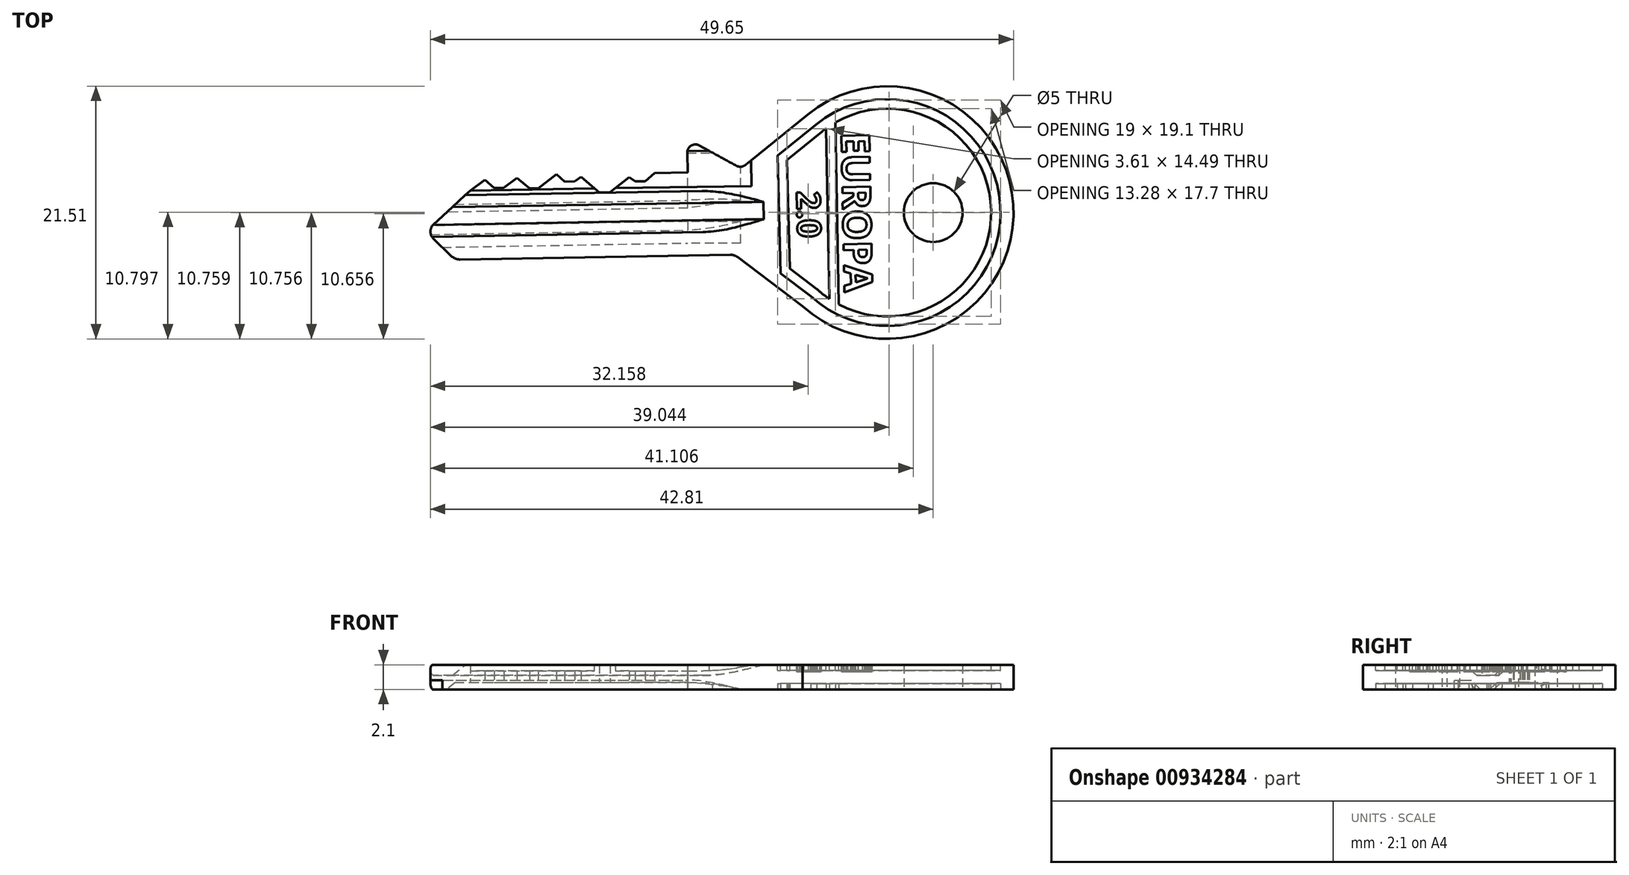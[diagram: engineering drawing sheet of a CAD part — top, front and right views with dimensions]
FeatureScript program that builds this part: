
annotation { "Feature Type Name" : "Feature", "Feature Type Description" : "" }
export const myFeature = defineFeature(function(context is Context, id is Id, definition is map)
    precondition{}
    {
        {
            var Q0;
            Q0=qCreatedBy(makeId("Top.planeOp"),FACE);
            var sketch = newSketch(context, id + "F0", { "sketchPlane" : qUnion([Q0])});
            skLineSegment(sketch, "E0", {"start": v(8, -3.49) * mm, "end": v(-15.02, -3.89) * mm});
            skLineSegment(sketch, "E1", {"start": v(-17.3, -2.08) * mm, "end": v(-15.74, -3.6) * mm});
            skPoint(sketch, "E2.visualSharp", {"position": v(-15.44, -3.9) * mm});
            skArc(sketch, "E2.filletArc", {"start": v(-15.74, -3.6) * mm, "mid": v(-15.41, -3.82) * mm, "end": v(-15.02, -3.89) * mm});
            skLineSegment(sketch, "E3", {"start": v(-14.14, 1.98) * mm, "end": v(-17.28, -0.92) * mm});
            skPoint(sketch, "E4.visualSharp", {"position": v(-17.9, -1.5) * mm});
            skArc(sketch, "E4.filletArc", {"start": v(-17.28, -0.92) * mm, "mid": v(-17.53, -1.5) * mm, "end": v(-17.3, -2.08) * mm});
            skLineSegment(sketch, "E5", {"start": v(-3.58, 2.18) * mm, "end": v(-14.14, 1.98) * mm});
            skLineSegment(sketch, "E6", {"start": v(1.54, 3.48) * mm, "end": v(4.36, 3.53) * mm});
            skLineSegment(sketch, "E7", {"start": v(4.36, 3.53) * mm, "end": v(4.33, 5.2) * mm});
            skLineSegment(sketch, "E8", {"start": v(8.52, 4.1) * mm, "end": v(5.37, 5.82) * mm});
            skPoint(sketch, "E9.visualSharp", {"position": v(4.3, 6.4) * mm});
            skArc(sketch, "E9.filletArc", {"start": v(5.37, 5.82) * mm, "mid": v(4.67, 5.8) * mm, "end": v(4.33, 5.2) * mm});
            skLineSegment(sketch, "E10", {"start": v(14.6, 8.46) * mm, "end": v(9.3, 4.16) * mm});
            skPoint(sketch, "E11.visualSharp", {"position": v(8.93, 3.87) * mm});
            skArc(sketch, "E11.filletArc", {"start": v(8.52, 4.1) * mm, "mid": v(8.92, 4.01) * mm, "end": v(9.3, 4.16) * mm});
            skLineSegment(sketch, "E12", {"start": v(15.16, -8.62) * mm, "end": v(8.63, -3.7) * mm});
            skPoint(sketch, "E13.visualSharp", {"position": v(8.35, -3.48) * mm});
            skArc(sketch, "E13.filletArc", {"start": v(8.63, -3.7) * mm, "mid": v(8.33, -3.54) * mm, "end": v(8, -3.49) * mm});
            skLineSegment(sketch, "E14", {"start": v(-0.61, 3.12) * mm, "end": v(-0.1, 2.75) * mm});
            skLineSegment(sketch, "E15", {"start": v(-0.1, 2.75) * mm, "end": v(0.75, 2.77) * mm});
            skLineSegment(sketch, "E16", {"start": v(0.75, 2.77) * mm, "end": v(1.54, 3.48) * mm});
            skLineSegment(sketch, "E17", {"start": v(-0.61, 3.12) * mm, "end": v(-2.21, 1.84) * mm});
            skLineSegment(sketch, "E18", {"start": v(-2.21, 1.84) * mm, "end": v(-3.15, 1.82) * mm});
            skLineSegment(sketch, "E19", {"start": v(-3.15, 1.82) * mm, "end": v(-4.72, 3.14) * mm});
            skLineSegment(sketch, "E20", {"start": v(-4.72, 3.14) * mm, "end": v(-5.24, 2.76) * mm});
            skLineSegment(sketch, "E21", {"start": v(-5.24, 2.76) * mm, "end": v(-6.1, 2.74) * mm});
            skLineSegment(sketch, "E22", {"start": v(-6.1, 2.74) * mm, "end": v(-6.8, 3.38) * mm});
            skLineSegment(sketch, "E23", {"start": v(-6.8, 3.38) * mm, "end": v(-8.35, 2.17) * mm});
            skLineSegment(sketch, "E24", {"start": v(-8.35, 2.17) * mm, "end": v(-9.1, 2.16) * mm});
            skLineSegment(sketch, "E25", {"start": v(-9.1, 2.16) * mm, "end": v(-10.17, 3.05) * mm});
            skLineSegment(sketch, "E26", {"start": v(-10.17, 3.05) * mm, "end": v(-11.26, 2.22) * mm});
            skLineSegment(sketch, "E27", {"start": v(-11.26, 2.22) * mm, "end": v(-12.1, 2.2) * mm});
            skLineSegment(sketch, "E28", {"start": v(-12.1, 2.2) * mm, "end": v(-12.9, 2.9) * mm});
            skLineSegment(sketch, "E29", {"start": v(-12.9, 2.9) * mm, "end": v(-14.14, 1.98) * mm});
            skArc(sketch, "E30", {"start": v(14.6, 8.46) * mm, "mid": v(32.11, -0.2) * mm, "end": v(14.15, -7.86) * mm});
            skCircle(sketch, "E31", {"center": v(25.28, 0.1) * mm, "radius": 2.5 * mm});
            skArc(sketch, "E32.0", {"start": v(15.3, 7.6) * mm, "mid": v(31.01, -0.18) * mm, "end": v(14.85, -7.01) * mm});
            skLineSegment(sketch, "E32.1", {"start": v(15.3, 7.6) * mm, "end": v(12.01, 4.95) * mm});
            skLineSegment(sketch, "E33.0", {"start": v(14.85, -7.01) * mm, "end": v(12.3, -5.08) * mm});
            skLineSegment(sketch, "E34", {"start": v(12.01, 4.95) * mm, "end": v(12.3, -5.08) * mm});
            skLineSegment(sketch, "E35", {"start": v(16.13, 8.21) * mm, "end": v(16.45, -8.2) * mm});
            skSolve(sketch);
        }
        {
            var Q0;
            Q0 = qSketchRegion(id + "F0", true);
            var Q1;
            Q1=makeQuery(id+"F0.imprint","IMPRINT",FACE,{"disambiguationData":[TD([[makeQuery(id+"F0.imprint","IMPRINT",EDGE,{"derivedFrom":sQuery(id+"F0.wireOp",EDGE,"E31")}),-1.0]])]});
            var Q2;
            {var subQ1=sQuery(id+"F0.wireOp",EDGE,"E32.1");Q2=makeQuery(id+"F0.imprint","IMPRINT",FACE,{"disambiguationData":[TD([[makeQuery(id+"F0.imprint","IMPRINT",EDGE,{"derivedFrom":subQ1}),1.0]])]});}
            extrude(context, id + "F1", {"entities" : qUnion([Q0, Q1, Q2]), "depth" : 2.1 * mm, "offsetDistance" : 25 * mm});
        }
        {
            var Q0;
            Q0=qCreatedBy(makeId("Top.planeOp"),FACE);
            var sketch = newSketch(context, id + "F2", { "sketchPlane" : qUnion([Q0])});
            skPoint(sketch, "E36.0", {"position": v(16.29, 0) * mm});
            skLineSegment(sketch, "E37.0", {"start": v(12.01, 4.95) * mm, "end": v(12.3, -5.08) * mm});
            skLineSegment(sketch, "E38.0", {"start": v(16.15, 7.25) * mm, "end": v(16.43, -7.24) * mm});
            skLineSegment(sketch, "E39.0", {"start": v(15.3, 7.6) * mm, "end": v(12.01, 4.95) * mm});
            skArc(sketch, "E40.0", {"start": v(15.3, 7.6) * mm, "mid": v(31.01, -0.18) * mm, "end": v(14.85, -7.01) * mm});
            skLineSegment(sketch, "E41.0", {"start": v(14.85, -7.01) * mm, "end": v(12.3, -5.08) * mm});
            skArc(sketch, "E42.0", {"start": v(15.8, 6.98) * mm, "mid": v(15.97, 7.12) * mm, "end": v(16.15, 7.25) * mm});
            skLineSegment(sketch, "E42.1", {"start": v(15.8, 6.98) * mm, "end": v(12.82, 4.58) * mm});
            skLineSegment(sketch, "E42.2", {"start": v(12.82, 4.58) * mm, "end": v(13.08, -4.67) * mm});
            skLineSegment(sketch, "E42.3", {"start": v(15.36, -6.4) * mm, "end": v(13.08, -4.67) * mm});
            skLineSegment(sketch, "E43.0", {"start": v(16.94, 7.77) * mm, "end": v(17.24, -7.72) * mm});
            skPoint(sketch, "E44.orphan", {"position": v(16.13, 8.21) * mm});
            skArc(sketch, "E45.trimOffspring", {"start": v(16.94, 7.77) * mm, "mid": v(30.22, 0.28) * mm, "end": v(17.24, -7.72) * mm});
            skPoint(sketch, "E46.orphan", {"position": v(16.45, -8.2) * mm});
            skArc(sketch, "E47.trimOffspring", {"start": v(16.43, -7.24) * mm, "mid": v(15.88, -6.84) * mm, "end": v(15.36, -6.4) * mm});
            skText(sketch, "E48", { "text": "EUROPA", "fontName": "OpenSans-Bold.ttf"});
            skLineSegment(sketch, "E49", {"start": v(17.35, 11.93) * mm, "end": v(17.85, -13.3) * mm, "construction": true});
            skPoint(sketch, "E50", {"position": v(17.45, 6.98) * mm});
            skText(sketch, "E51", { "text": "2.0", "fontName": "OpenSans-Bold.ttf"});
            skPoint(sketch, "E52", {"position": v(12.88, 2.46) * mm});
            const initialGuessF2  = {"E48": [0.01745, 0.00698, 0.01969, -0.9998, 0.0024], "E51": [0.01288, 0.00246, 0.0276, -0.99962, 0.0024]};
            skSetInitialGuess(sketch, initialGuessF2);
            skSolve(sketch);
        }
        {
            var Q0;
            Q0 = qSketchRegion(id + "F2", true);
            extrude(context, id + "F3", {"entities" : qUnion([Q0]), "operationType" : NewBodyOperationType.REMOVE, "depth" : 0.5 * mm, "offsetDistance" : 25 * mm});
        }
        {
            var Q0;
            Q0=makeQuery(id+"F1.opExtrude","CAP_FACE",FACE,{"disambiguationData":[OSD([sQuery(id+"F0.wireOp",EDGE,"E0"),sQuery(id+"F0.wireOp",EDGE,"E1"),sQuery(id+"F0.wireOp",EDGE,"E2.filletArc"),sQuery(id+"F0.wireOp",EDGE,"E3"),sQuery(id+"F0.wireOp",EDGE,"E4.filletArc"),sQuery(id+"F0.wireOp",EDGE,"E6"),sQuery(id+"F0.wireOp",EDGE,"E7"),sQuery(id+"F0.wireOp",EDGE,"E8"),sQuery(id+"F0.wireOp",EDGE,"E9.filletArc"),sQuery(id+"F0.wireOp",EDGE,"E10"),sQuery(id+"F0.wireOp",EDGE,"E11.filletArc"),sQuery(id+"F0.wireOp",EDGE,"E12"),sQuery(id+"F0.wireOp",EDGE,"E13.filletArc"),sQuery(id+"F0.wireOp",EDGE,"E14"),sQuery(id+"F0.wireOp",EDGE,"E15"),sQuery(id+"F0.wireOp",EDGE,"E16"),sQuery(id+"F0.wireOp",EDGE,"E17"),sQuery(id+"F0.wireOp",EDGE,"E18"),sQuery(id+"F0.wireOp",EDGE,"E19"),sQuery(id+"F0.wireOp",EDGE,"E20"),sQuery(id+"F0.wireOp",EDGE,"E21"),sQuery(id+"F0.wireOp",EDGE,"E22"),sQuery(id+"F0.wireOp",EDGE,"E23"),sQuery(id+"F0.wireOp",EDGE,"E24"),sQuery(id+"F0.wireOp",EDGE,"E25"),sQuery(id+"F0.wireOp",EDGE,"E26"),sQuery(id+"F0.wireOp",EDGE,"E27"),sQuery(id+"F0.wireOp",EDGE,"E28"),sQuery(id+"F0.wireOp",EDGE,"E29"),sQuery(id+"F0.wireOp",EDGE,"E30"),sQuery(id+"F0.wireOp",EDGE,"E31")])],"isStart":false});
            var sketch = newSketch(context, id + "F4", { "sketchPlane" : qUnion([Q0])});
            skArc(sketch, "E53.0", {"start": v(15.3, 7.6) * mm, "mid": v(31.01, -0.18) * mm, "end": v(14.85, -7.01) * mm});
            skArc(sketch, "E54.0", {"start": v(16.94, 7.77) * mm, "mid": v(30.22, 0.28) * mm, "end": v(17.24, -7.72) * mm});
            skLineSegment(sketch, "E55.0", {"start": v(15.3, 7.6) * mm, "end": v(12.01, 4.95) * mm});
            skLineSegment(sketch, "E56.0", {"start": v(12.01, 4.95) * mm, "end": v(12.3, -5.08) * mm});
            skLineSegment(sketch, "E57.0", {"start": v(14.85, -7.01) * mm, "end": v(12.3, -5.08) * mm});
            skLineSegment(sketch, "E58.0", {"start": v(12.82, 4.58) * mm, "end": v(13.08, -4.67) * mm});
            skLineSegment(sketch, "E59.0", {"start": v(15.36, -6.4) * mm, "end": v(13.08, -4.67) * mm});
            skLineSegment(sketch, "E60.0", {"start": v(15.8, 6.98) * mm, "end": v(12.82, 4.58) * mm});
            skLineSegment(sketch, "E61.0", {"start": v(16.15, 7.25) * mm, "end": v(16.43, -7.24) * mm});
            skArc(sketch, "E62.0", {"start": v(16.43, -7.24) * mm, "mid": v(15.88, -6.84) * mm, "end": v(15.36, -6.4) * mm});
            skArc(sketch, "E63.0", {"start": v(15.8, 6.98) * mm, "mid": v(15.97, 7.12) * mm, "end": v(16.15, 7.25) * mm});
            skLineSegment(sketch, "E64.0", {"start": v(16.94, 7.77) * mm, "end": v(17.24, -7.72) * mm});
            skSolve(sketch);
        }
        {
            var Q0;
            Q0 = qSketchRegion(id + "F4", true);
            extrude(context, id + "F5", {"entities" : qUnion([Q0]), "operationType" : NewBodyOperationType.REMOVE, "oppositeDirection" : true, "depth" : 0.5 * mm, "offsetDistance" : 25 * mm});
        }
        {
            var Q0;
            {var subQ0=sQuery(id+"F0.wireOp",EDGE,"E21");var subQ1=sQuery(id+"F0.wireOp",EDGE,"E20");var subQ2=sQuery(id+"F0.wireOp",EDGE,"E19");var subQ3=sQuery(id+"F0.wireOp",EDGE,"E18");var subQ4=sQuery(id+"F0.wireOp",EDGE,"E17");var subQ5=sQuery(id+"F0.wireOp",EDGE,"E16");var subQ6=sQuery(id+"F0.wireOp",EDGE,"E15");var subQ7=sQuery(id+"F0.wireOp",EDGE,"E14");var subQ8=sQuery(id+"F0.wireOp",EDGE,"E13.filletArc");var subQ9=sQuery(id+"F0.wireOp",EDGE,"E12");var subQ10=sQuery(id+"F0.wireOp",EDGE,"E11.filletArc");var subQ11=sQuery(id+"F0.wireOp",EDGE,"E2.filletArc");var subQ12=sQuery(id+"F0.wireOp",EDGE,"E1");var subQ13=sQuery(id+"F0.wireOp",EDGE,"E3");var subQ14=sQuery(id+"F0.wireOp",EDGE,"E22");var subQ15=sQuery(id+"F0.wireOp",EDGE,"E0");var subQ16=sQuery(id+"F0.wireOp",EDGE,"E10");var subQ17=sQuery(id+"F0.wireOp",EDGE,"E4.filletArc");var subQ18=sQuery(id+"F0.wireOp",EDGE,"E6");var subQ19=sQuery(id+"F0.wireOp",EDGE,"E7");var subQ20=sQuery(id+"F0.wireOp",EDGE,"E8");var subQ21=sQuery(id+"F0.wireOp",EDGE,"E9.filletArc");var subQ22=sQuery(id+"F0.wireOp",EDGE,"E23");var subQ23=sQuery(id+"F0.wireOp",EDGE,"E24");var subQ24=sQuery(id+"F0.wireOp",EDGE,"E25");var subQ25=sQuery(id+"F0.wireOp",EDGE,"E26");var subQ26=sQuery(id+"F0.wireOp",EDGE,"E27");var subQ27=sQuery(id+"F0.wireOp",EDGE,"E28");var subQ28=sQuery(id+"F0.wireOp",EDGE,"E29");var subQ29=sQuery(id+"F0.wireOp",EDGE,"E30");Q0=makeQuery(id+"F5.boolean.opBoolean","SPLIT",FACE,{"disambiguationData":[TD([makeQuery(id+"F1.opExtrude","SWEPT_FACE",FACE,{"disambiguationData":[OSD([subQ15])]})])],"derivedFrom":makeQuery(id+"F1.opExtrude","CAP_FACE",FACE,{"disambiguationData":[OSD([subQ15,subQ12,subQ11,subQ13,subQ17,subQ18,subQ19,subQ20,subQ21,subQ16,subQ10,subQ9,subQ8,subQ7,subQ6,subQ5,subQ4,subQ3,subQ2,subQ1,subQ0,subQ14,subQ22,subQ23,subQ24,subQ25,subQ26,subQ27,subQ28,subQ29,sQuery(id+"F0.wireOp",EDGE,"E31")])],"isStart":false})});}
            var sketch = newSketch(context, id + "F6", { "sketchPlane" : qUnion([Q0])});
            skLineSegment(sketch, "E65", {"start": v(-22.93, -1.04) * mm, "end": v(5.65, -0.55) * mm});
            skLineSegment(sketch, "E66", {"start": v(5.65, -0.55) * mm, "end": v(5.63, 0.93) * mm});
            skLineSegment(sketch, "E67", {"start": v(5.63, 0.93) * mm, "end": v(-22.93, 0.44) * mm});
            skLineSegment(sketch, "E68", {"start": v(-22.93, 0.44) * mm, "end": v(-22.93, -1.04) * mm});
            skSolve(sketch);
        }
        {
            var Q0;
            {var subQ0=sQuery(id+"F0.wireOp",EDGE,"E21");var subQ1=sQuery(id+"F0.wireOp",EDGE,"E20");var subQ2=sQuery(id+"F0.wireOp",EDGE,"E19");var subQ3=sQuery(id+"F0.wireOp",EDGE,"E18");var subQ4=sQuery(id+"F0.wireOp",EDGE,"E17");var subQ5=sQuery(id+"F0.wireOp",EDGE,"E16");var subQ6=sQuery(id+"F0.wireOp",EDGE,"E15");var subQ7=sQuery(id+"F0.wireOp",EDGE,"E14");var subQ8=sQuery(id+"F0.wireOp",EDGE,"E13.filletArc");var subQ9=sQuery(id+"F0.wireOp",EDGE,"E12");var subQ10=sQuery(id+"F0.wireOp",EDGE,"E11.filletArc");var subQ11=sQuery(id+"F0.wireOp",EDGE,"E2.filletArc");var subQ12=sQuery(id+"F0.wireOp",EDGE,"E1");var subQ13=sQuery(id+"F0.wireOp",EDGE,"E3");var subQ14=sQuery(id+"F0.wireOp",EDGE,"E22");var subQ15=sQuery(id+"F0.wireOp",EDGE,"E0");var subQ16=sQuery(id+"F0.wireOp",EDGE,"E10");var subQ17=sQuery(id+"F0.wireOp",EDGE,"E4.filletArc");var subQ18=sQuery(id+"F0.wireOp",EDGE,"E6");var subQ19=sQuery(id+"F0.wireOp",EDGE,"E7");var subQ20=sQuery(id+"F0.wireOp",EDGE,"E8");var subQ21=sQuery(id+"F0.wireOp",EDGE,"E9.filletArc");var subQ22=sQuery(id+"F0.wireOp",EDGE,"E23");var subQ23=sQuery(id+"F0.wireOp",EDGE,"E24");var subQ24=sQuery(id+"F0.wireOp",EDGE,"E25");var subQ25=sQuery(id+"F0.wireOp",EDGE,"E26");var subQ26=sQuery(id+"F0.wireOp",EDGE,"E27");var subQ27=sQuery(id+"F0.wireOp",EDGE,"E28");var subQ28=sQuery(id+"F0.wireOp",EDGE,"E29");var subQ29=sQuery(id+"F0.wireOp",EDGE,"E30");Q0=makeQuery(id+"F5.boolean.opBoolean","SPLIT",FACE,{"disambiguationData":[TD([makeQuery(id+"F1.opExtrude","SWEPT_FACE",FACE,{"disambiguationData":[OSD([subQ15])]})])],"derivedFrom":makeQuery(id+"F1.opExtrude","CAP_FACE",FACE,{"disambiguationData":[OSD([subQ15,subQ12,subQ11,subQ13,subQ17,subQ18,subQ19,subQ20,subQ21,subQ16,subQ10,subQ9,subQ8,subQ7,subQ6,subQ5,subQ4,subQ3,subQ2,subQ1,subQ0,subQ14,subQ22,subQ23,subQ24,subQ25,subQ26,subQ27,subQ28,subQ29,sQuery(id+"F0.wireOp",EDGE,"E31")])],"isStart":false})});}
            var sketch = newSketch(context, id + "F7", { "sketchPlane" : qUnion([Q0])});
            skLineSegment(sketch, "E69", {"start": v(-14.65, 1.98) * mm, "end": v(4.42, 2.28) * mm});
            skLineSegment(sketch, "E70", {"start": v(4.42, 2.28) * mm, "end": v(4.35, 6.53) * mm});
            skLineSegment(sketch, "E71", {"start": v(4.35, 6.53) * mm, "end": v(-14.58, 4.95) * mm});
            skLineSegment(sketch, "E72", {"start": v(-14.58, 4.95) * mm, "end": v(-14.65, 1.98) * mm});
            skSolve(sketch);
        }
        {
            var Q0;
            Q0 = qSketchRegion(id + "F7", true);
            extrude(context, id + "F8", {"entities" : qUnion([Q0]), "operationType" : NewBodyOperationType.REMOVE, "oppositeDirection" : true, "depth" : 0.52 * mm, "offsetDistance" : 25 * mm});
        }
        {
            var Q0;
            {var subQ0=sQuery(id+"F0.wireOp",EDGE,"E17");var subQ2=sQuery(id+"F7.wireOp",EDGE,"E69");Q0=makeQuery(id+"F8.boolean.opBoolean","COPY",FACE,{"disambiguationData":[TD([makeQuery(id+"F1.opExtrude","SWEPT_FACE",FACE,{"disambiguationData":[OSD([subQ0])]})])],"derivedFrom":makeQuery(id+"F8.opExtrude","SWEPT_FACE",FACE,{"disambiguationData":[OSD([subQ2])]})});}
            var sketch = newSketch(context, id + "F9", { "sketchPlane" : qUnion([Q0])});
            skLineSegment(sketch, "E73.0", {"start": v(-4.45, 1.58) * mm, "end": v(-4.45, 2.1) * mm});
            skLineSegment(sketch, "E74", {"start": v(-4.45, 1.58) * mm, "end": v(-9.85, 1.58) * mm});
            skLineSegment(sketch, "E75", {"start": v(-4.45, 2.1) * mm, "end": v(-4.45, 2.45) * mm});
            skLineSegment(sketch, "E76", {"start": v(-4.45, 2.45) * mm, "end": v(-9.85, 2.62) * mm});
            skLineSegment(sketch, "E77", {"start": v(-9.85, 2.62) * mm, "end": v(-9.85, 1.58) * mm});
            skPoint(sketch, "E78", {"position": v(-9.85, 2.1) * mm});
            skFitSpline(sketch, "E79", {"points": [v(-4.45, 1.58) * mm, v(-9.85, 2.1) * mm], "startDerivative": vector(-6.66, 0) * mm, "endDerivative": vector(-5.03, 1.26) * mm});
            skSolve(sketch);
        }
        {
            var Q0;
            Q0=makeQuery(id+"F9.imprint","IMPRINT",FACE,{"disambiguationData":[TD([[makeQuery(id+"F9.imprint","IMPRINT",EDGE,{"derivedFrom":sQuery(id+"F9.wireOp",EDGE,"E73.0")}),1.0]])]});
            extrude(context, id + "F10", {"entities" : qUnion([Q0]), "operationType" : NewBodyOperationType.REMOVE, "depth" : 3.06 * mm, "offsetDistance" : 25 * mm});
        }
        {
            var Q0;
            {var subQ0=sQuery(id+"F0.wireOp",EDGE,"E21");var subQ1=sQuery(id+"F0.wireOp",EDGE,"E20");var subQ2=sQuery(id+"F0.wireOp",EDGE,"E19");var subQ3=sQuery(id+"F0.wireOp",EDGE,"E18");var subQ4=sQuery(id+"F0.wireOp",EDGE,"E17");var subQ5=sQuery(id+"F0.wireOp",EDGE,"E16");var subQ6=sQuery(id+"F0.wireOp",EDGE,"E15");var subQ7=sQuery(id+"F0.wireOp",EDGE,"E14");var subQ8=sQuery(id+"F0.wireOp",EDGE,"E13.filletArc");var subQ9=sQuery(id+"F0.wireOp",EDGE,"E12");var subQ10=sQuery(id+"F0.wireOp",EDGE,"E11.filletArc");var subQ11=sQuery(id+"F0.wireOp",EDGE,"E2.filletArc");var subQ12=sQuery(id+"F0.wireOp",EDGE,"E1");var subQ13=sQuery(id+"F0.wireOp",EDGE,"E3");var subQ14=sQuery(id+"F0.wireOp",EDGE,"E22");var subQ15=sQuery(id+"F0.wireOp",EDGE,"E0");var subQ16=sQuery(id+"F0.wireOp",EDGE,"E10");var subQ17=sQuery(id+"F0.wireOp",EDGE,"E4.filletArc");var subQ18=sQuery(id+"F0.wireOp",EDGE,"E6");var subQ19=sQuery(id+"F0.wireOp",EDGE,"E7");var subQ20=sQuery(id+"F0.wireOp",EDGE,"E8");var subQ21=sQuery(id+"F0.wireOp",EDGE,"E9.filletArc");var subQ22=sQuery(id+"F0.wireOp",EDGE,"E23");var subQ23=sQuery(id+"F0.wireOp",EDGE,"E24");var subQ24=sQuery(id+"F0.wireOp",EDGE,"E25");var subQ25=sQuery(id+"F0.wireOp",EDGE,"E26");var subQ26=sQuery(id+"F0.wireOp",EDGE,"E27");var subQ27=sQuery(id+"F0.wireOp",EDGE,"E28");var subQ28=sQuery(id+"F0.wireOp",EDGE,"E29");var subQ29=sQuery(id+"F0.wireOp",EDGE,"E30");Q0=makeQuery(id+"F3.boolean.opBoolean","SPLIT",FACE,{"disambiguationData":[TD([makeQuery(id+"F1.opExtrude","SWEPT_FACE",FACE,{"disambiguationData":[OSD([subQ15])]})])],"derivedFrom":makeQuery(id+"F1.opExtrude","CAP_FACE",FACE,{"disambiguationData":[OSD([subQ15,subQ12,subQ11,subQ13,subQ17,subQ18,subQ19,subQ20,subQ21,subQ16,subQ10,subQ9,subQ8,subQ7,subQ6,subQ5,subQ4,subQ3,subQ2,subQ1,subQ0,subQ14,subQ22,subQ23,subQ24,subQ25,subQ26,subQ27,subQ28,subQ29,sQuery(id+"F0.wireOp",EDGE,"E31")])],"isStart":true})});}
            var sketch = newSketch(context, id + "F11", { "sketchPlane" : qUnion([Q0])});
            skArc(sketch, "E80.0", {"start": v(5.37, -5.82) * mm, "mid": v(4.67, -5.8) * mm, "end": v(4.33, -5.2) * mm});
            skLineSegment(sketch, "E81", {"start": v(1.71, -5.85) * mm, "end": v(7.72, -5.95) * mm, "construction": true});
            skLineSegment(sketch, "E82", {"start": v(1.2, -4.59) * mm, "end": v(8.54, -4.72) * mm, "construction": true});
            skLineSegment(sketch, "E83.0", {"start": v(4.36, -3.53) * mm, "end": v(4.33, -5.2) * mm});
            skLineSegment(sketch, "E84", {"start": v(4.35, -4.36) * mm, "end": v(-15.49, -4.02) * mm});
            skLineSegment(sketch, "E85", {"start": v(-15.49, -4.02) * mm, "end": v(-15.42, -0.8) * mm});
            skLineSegment(sketch, "E86", {"start": v(-15.42, -0.8) * mm, "end": v(4.36, -1.14) * mm});
            skLineSegment(sketch, "E87", {"start": v(4.36, -1.14) * mm, "end": v(4.36, -3.53) * mm});
            skLineSegment(sketch, "E88", {"start": v(4.36, -1.14) * mm, "end": v(7, -2.33) * mm});
            skLineSegment(sketch, "E89", {"start": v(7, -2.33) * mm, "end": v(7, -4.93) * mm});
            skLineSegment(sketch, "E90.0", {"start": v(8.52, -4.1) * mm, "end": v(5.37, -5.82) * mm});
            skLineSegment(sketch, "E91", {"start": v(7, -4.93) * mm, "end": v(4.34, -4.88) * mm});
            skSolve(sketch);
        }
        {
            var Q0;
            {var subQ2=sQuery(id+"F11.wireOp",EDGE,"E84");Q0=makeQuery(id+"F11.imprint","IMPRINT",FACE,{"disambiguationData":[TD([[makeQuery(id+"F11.imprint","IMPRINT",EDGE,{"derivedFrom":subQ2}),-1.0]])]});}
            var Q1;
            {var subQ0=sQuery(id+"F11.wireOp",EDGE,"E87");Q1=makeQuery(id+"F11.imprint","IMPRINT",FACE,{"disambiguationData":[TD([[makeQuery(id+"F11.imprint","IMPRINT",EDGE,{"derivedFrom":subQ0}),-1.0]])]});}
            extrude(context, id + "F12", {"entities" : qUnion([Q0, Q1]), "operationType" : NewBodyOperationType.REMOVE, "oppositeDirection" : true, "depth" : 0.59 * mm, "offsetDistance" : 25 * mm});
        }
        {
            var Q0;
            Q0 = qSketchRegion(id + "F6", true);
            extrude(context, id + "F13", {"entities" : qUnion([Q0]), "operationType" : NewBodyOperationType.REMOVE, "oppositeDirection" : true, "depth" : 0.91 * mm, "offsetDistance" : 25 * mm});
        }
        {
            var Q0;
            Q0=makeQuery(id+"F13.boolean.opBoolean","COPY",FACE,{"derivedFrom":makeQuery(id+"F13.opExtrude","SWEPT_FACE",FACE,{"disambiguationData":[OSD([sQuery(id+"F6.wireOp",EDGE,"E66")])]})});
            var sketch = newSketch(context, id + "F14", { "sketchPlane" : qUnion([Q0])});
            skLineSegment(sketch, "E92.0", {"start": v(-0.83, 1.2) * mm, "end": v(-0.83, 2.1) * mm});
            skLineSegment(sketch, "E93.0", {"start": v(0.65, 1.2) * mm, "end": v(0.65, 2.1) * mm});
            skLineSegment(sketch, "E94", {"start": v(-0.83, 2.1) * mm, "end": v(-1.83, 2.1) * mm});
            skLineSegment(sketch, "E95", {"start": v(0.65, 2.1) * mm, "end": v(1.65, 2.1) * mm});
            skLineSegment(sketch, "E96", {"start": v(-0.83, 1.2) * mm, "end": v(-1.83, 2.1) * mm});
            skLineSegment(sketch, "E97", {"start": v(0.65, 1.2) * mm, "end": v(1.65, 2.1) * mm});
            skSolve(sketch);
        }
        {
            var Q0;
            Q0 = qSketchRegion(id + "F14", true);
            extrude(context, id + "F15", {"entities" : qUnion([Q0]), "operationType" : NewBodyOperationType.REMOVE, "depth" : 40 * mm, "offsetDistance" : 25 * mm});
        }
        {
            var Q0;
            Q0=makeQuery(id+"F15.boolean.opBoolean","MERGE",FACE,{"derivedFrom":[makeQuery(id+"F13.boolean.opBoolean","COPY",FACE,{"derivedFrom":makeQuery(id+"F13.opExtrude","SWEPT_FACE",FACE,{"disambiguationData":[OSD([sQuery(id+"F6.wireOp",EDGE,"E66")])]})})],"fromTools":[makeQuery(id+"F15.opExtrude","CAP_FACE",FACE,{"disambiguationData":[OSD([sQuery(id+"F14.wireOp",EDGE,"E92.0"),sQuery(id+"F14.wireOp",EDGE,"E94"),sQuery(id+"F14.wireOp",EDGE,"E96")])],"isStart":true}),makeQuery(id+"F15.opExtrude","CAP_FACE",FACE,{"disambiguationData":[OSD([sQuery(id+"F14.wireOp",EDGE,"E93.0"),sQuery(id+"F14.wireOp",EDGE,"E95"),sQuery(id+"F14.wireOp",EDGE,"E97")])],"isStart":true})]});
            cPlane(context, id + "F16", {"entities" : qUnion([Q0]), "cplaneType" : CPlaneType.OFFSET, "offset" : 5.2 * mm, "oppositeDirection" : true, "width" : 150 * mm, "height" : 150 * mm});
        }
        {
            var Q0;
            Q0=qCreatedBy(id+"F16.planeOp",FACE);
            var sketch = newSketch(context, id + "F17", { "sketchPlane" : qUnion([Q0])});
            skLineSegment(sketch, "E98.0", {"start": v(0.65, 2.1) * mm, "end": v(-0.83, 2.1) * mm});
            skLineSegment(sketch, "E99", {"start": v(-0.83, 2.1) * mm, "end": v(-1.83, 3.01) * mm});
            skLineSegment(sketch, "E100", {"start": v(-1.83, 3.01) * mm, "end": v(1.65, 3.01) * mm});
            skLineSegment(sketch, "E101", {"start": v(1.65, 3.01) * mm, "end": v(0.65, 2.1) * mm});
            skLineSegment(sketch, "E102.0", {"start": v(0.65, 1.2) * mm, "end": v(-0.83, 1.2) * mm});
            skLineSegment(sketch, "E103", {"start": v(-0.83, 0.8) * mm, "end": v(-0.83, 3.67) * mm, "construction": true});
            skSolve(sketch);
        }
        {
            var Q0;
            Q0=makeQuery(id+"F15.boolean.opBoolean","MERGE",FACE,{"derivedFrom":[makeQuery(id+"F13.boolean.opBoolean","COPY",FACE,{"derivedFrom":makeQuery(id+"F13.opExtrude","SWEPT_FACE",FACE,{"disambiguationData":[OSD([sQuery(id+"F6.wireOp",EDGE,"E66")])]})})],"fromTools":[makeQuery(id+"F15.opExtrude","CAP_FACE",FACE,{"disambiguationData":[OSD([sQuery(id+"F14.wireOp",EDGE,"E92.0"),sQuery(id+"F14.wireOp",EDGE,"E94"),sQuery(id+"F14.wireOp",EDGE,"E96")])],"isStart":true}),makeQuery(id+"F15.opExtrude","CAP_FACE",FACE,{"disambiguationData":[OSD([sQuery(id+"F14.wireOp",EDGE,"E93.0"),sQuery(id+"F14.wireOp",EDGE,"E95"),sQuery(id+"F14.wireOp",EDGE,"E97")])],"isStart":true})]});
            var sketch = newSketch(context, id + "F18", { "sketchPlane" : qUnion([Q0])});
            skLineSegment(sketch, "E104.0", {"start": v(-0.83, 1.2) * mm, "end": v(-1.83, 2.1) * mm});
            skLineSegment(sketch, "E105.0", {"start": v(1.65, 2.1) * mm, "end": v(-1.83, 2.1) * mm});
            skLineSegment(sketch, "E106.0", {"start": v(0.65, 1.2) * mm, "end": v(-0.83, 1.2) * mm});
            skLineSegment(sketch, "E107.0", {"start": v(0.65, 1.19) * mm, "end": v(1.65, 2.1) * mm});
            skSolve(sketch);
        }
        {
            var Q1;
            Q1 = qSketchRegion(id + "F18", true);
            var Q2;
            Q2 = qSketchRegion(id + "F17", true);
            loft(context, id + "F19", {"operationType" : NewBodyOperationType.REMOVE, "startCondition" : LoftEndDerivativeType.NORMAL_TO_PROFILE, "startMagnitude" : 1, "sheetProfilesArray" : [{ "sheetProfileEntities" : qUnion([Q1]) }, { "sheetProfileEntities" : qUnion([Q2]) }]});
        }
        {
            var Q0;
            Q0=makeQuery(id+"F12.boolean.opBoolean","COPY",FACE,{"derivedFrom":makeQuery(id+"F12.opExtrude","CAP_FACE",FACE,{"disambiguationData":[OSD([sQuery(id+"F11.wireOp",EDGE,"E83.0"),sQuery(id+"F11.wireOp",EDGE,"E84"),sQuery(id+"F11.wireOp",EDGE,"E85"),sQuery(id+"F11.wireOp",EDGE,"E86"),sQuery(id+"F11.wireOp",EDGE,"E87")])],"isStart":false})});
            var sketch = newSketch(context, id + "F20", { "sketchPlane" : qUnion([Q0])});
            skLineSegment(sketch, "E108.0", {"start": v(-18.14, -0.75) * mm, "end": v(4.36, -1.14) * mm});
            skPoint(sketch, "E109.orphan", {"position": v(-15.41, -0.8) * mm});
            skSolve(sketch);
        }
        {
            var Q0;
            Q0=makeQuery(id+"F12.boolean.opBoolean","COPY",FACE,{"derivedFrom":makeQuery(id+"F12.opExtrude","SWEPT_FACE",FACE,{"disambiguationData":[OSD([sQuery(id+"F11.wireOp",EDGE,"E87")])]})});
            var sketch = newSketch(context, id + "F21", { "sketchPlane" : qUnion([Q0])});
            skLineSegment(sketch, "E110.0", {"start": v(-1.14, 0.6) * mm, "end": v(-1.14, 0) * mm});
            skLineSegment(sketch, "E111", {"start": v(-1.14, 0) * mm, "end": v(-0.5, 0) * mm});
            skLineSegment(sketch, "E112", {"start": v(-0.5, 0) * mm, "end": v(-1.14, 0.6) * mm});
            skSolve(sketch);
        }
        {
            var Q0;
            Q0 = qSketchRegion(id + "F21", true);
            var Q1;
            Q1=sQuery(id+"F20.wireOp",EDGE,"E108.0");
            sweep(context, id + "F22", {"operationType" : NewBodyOperationType.REMOVE, "profiles" : qUnion([Q0]), "path" : qUnion([Q1])});
        }
        {
            var Q0;
            Q0=makeQuery(id+"F22.boolean.opBoolean","MERGE",FACE,{"derivedFrom":[makeQuery(id+"F12.boolean.opBoolean","COPY",FACE,{"derivedFrom":makeQuery(id+"F12.opExtrude","SWEPT_FACE",FACE,{"disambiguationData":[OSD([sQuery(id+"F11.wireOp",EDGE,"E87")])]})})],"fromTools":[makeQuery(id+"F22.opSweep","CAP_FACE",FACE,{"disambiguationData":[OSD([sQuery(id+"F20.wireOp",VERTEX,"E108.0.end"),sQuery(id+"F21.wireOp",EDGE,"E110.0"),sQuery(id+"F21.wireOp",EDGE,"E111"),sQuery(id+"F21.wireOp",EDGE,"E112")])],"isStart":true})]});
            cPlane(context, id + "F23", {"entities" : qUnion([Q0]), "cplaneType" : CPlaneType.OFFSET, "offset" : 4.52 * mm, "oppositeDirection" : true, "width" : 150 * mm, "height" : 150 * mm});
        }
        {
            var Q0;
            Q0=qCreatedBy(id+"F23.planeOp",FACE);
            var sketch = newSketch(context, id + "F24", { "sketchPlane" : qUnion([Q0])});
            skLineSegment(sketch, "E113.0", {"start": v(-1.14, 0.6) * mm, "end": v(-3.53, 0.6) * mm});
            skLineSegment(sketch, "E114", {"start": v(-1.14, 1.38) * mm, "end": v(-1.14, -2) * mm, "construction": true});
            skLineSegment(sketch, "E115", {"start": v(-3.53, 1.4) * mm, "end": v(-3.53, 0) * mm, "construction": true});
            skLineSegment(sketch, "E116", {"start": v(-0.5, -0.59) * mm, "end": v(-1.14, 0) * mm});
            skLineSegment(sketch, "E117.0", {"start": v(-5.2, 0) * mm, "end": v(-5.2, -0.6) * mm});
            skLineSegment(sketch, "E118.trimOffspring", {"start": v(-3.53, -0.6) * mm, "end": v(-3.53, -2.08) * mm, "construction": true});
            skPoint(sketch, "E119.orphan", {"position": v(-5.2, 1.58) * mm});
            skLineSegment(sketch, "E120", {"start": v(-1.14, 0) * mm, "end": v(-5.2, 0) * mm});
            skLineSegment(sketch, "E121", {"start": v(-0.5, -0.59) * mm, "end": v(-5.2, -0.6) * mm});
            skSolve(sketch);
        }
        {
            var Q0;
            Q0=makeQuery(id+"F22.boolean.opBoolean","MERGE",FACE,{"derivedFrom":[makeQuery(id+"F12.boolean.opBoolean","COPY",FACE,{"derivedFrom":makeQuery(id+"F12.opExtrude","SWEPT_FACE",FACE,{"disambiguationData":[OSD([sQuery(id+"F11.wireOp",EDGE,"E87")])]})})],"fromTools":[makeQuery(id+"F22.opSweep","CAP_FACE",FACE,{"disambiguationData":[OSD([sQuery(id+"F20.wireOp",VERTEX,"E108.0.end"),sQuery(id+"F21.wireOp",EDGE,"E110.0"),sQuery(id+"F21.wireOp",EDGE,"E111"),sQuery(id+"F21.wireOp",EDGE,"E112")])],"isStart":true})]});
            var sketch = newSketch(context, id + "F25", { "sketchPlane" : qUnion([Q0])});
            skLineSegment(sketch, "E122.0", {"start": v(-0.5, 0) * mm, "end": v(-1.14, 0.6) * mm});
            skLineSegment(sketch, "E123.0", {"start": v(-5.2, 0.6) * mm, "end": v(-5.2, 0) * mm});
            skPoint(sketch, "E124.orphan", {"position": v(-5.2, 1.58) * mm});
            skLineSegment(sketch, "E125", {"start": v(-0.5, 0) * mm, "end": v(-5.2, 0) * mm});
            skLineSegment(sketch, "E126", {"start": v(-5.2, 0.6) * mm, "end": v(-1.14, 0.6) * mm});
            skSolve(sketch);
        }
        {
            var Q0;
            Q0=sQuery(id+"F25.wireOp",VERTEX,"E123.0.end");
            var Q1;
            Q1=sQuery(id+"F24.wireOp",VERTEX,"E117.0.end");
            var Q2;
            Q2=sQuery(id+"F24.wireOp",VERTEX,"E117.0.start");
            cPlane(context, id + "F26", {"entities" : qUnion([Q0, Q1, Q2]), "cplaneType" : CPlaneType.THREE_POINT, "offset" : 25 * mm, "width" : 150 * mm, "height" : 150 * mm});
        }
        {
            var Q0;
            Q0=qCreatedBy(id+"F26.planeOp",FACE);
            var sketch = newSketch(context, id + "F27", { "sketchPlane" : qUnion([Q0])});
            skPoint(sketch, "E127.0", {"position": v(-4.36, 0) * mm});
            skPoint(sketch, "E128.0", {"position": v(-8.88, -0.6) * mm});
            skPoint(sketch, "E129.0", {"position": v(-8.88, 0) * mm});
            skPoint(sketch, "E130.0", {"position": v(-4.36, 0.6) * mm});
            skLineSegment(sketch, "E131", {"start": v(-4.36, 0) * mm, "end": v(-4.36, 0.6) * mm, "construction": true});
            skLineSegment(sketch, "E132", {"start": v(-8.88, -0.6) * mm, "end": v(-8.88, 0) * mm, "construction": true});
            skLineSegment(sketch, "E133", {"start": v(-5.71, 0) * mm, "end": v(-4.36, 0) * mm, "construction": true});
            skLineSegment(sketch, "E134", {"start": v(-4.36, 0.59) * mm, "end": v(-5.8, 0.59) * mm, "construction": true});
            skFitSpline(sketch, "E135", {"points": [v(-4.36, 0.6) * mm, v(-8.88, 0) * mm], "startDerivative": vector(-6.52, 0) * mm, "endDerivative": vector(-4.26, -1.3) * mm});
            skFitSpline(sketch, "E136", {"points": [v(-4.36, 0) * mm, v(-8.88, -0.6) * mm], "startDerivative": vector(-6.56, 0) * mm, "endDerivative": vector(-4.45, -1.16) * mm});
            skSolve(sketch);
        }
        {
            var Q0;
            Q0=sQuery(id+"F25.wireOp",VERTEX,"E122.0.start");
            var Q1;
            Q1=sQuery(id+"F24.wireOp",VERTEX,"E116.start");
            var Q2;
            Q2=sQuery(id+"F24.wireOp",VERTEX,"E116.end");
            cPlane(context, id + "F28", {"entities" : qUnion([Q0, Q1, Q2]), "cplaneType" : CPlaneType.THREE_POINT, "offset" : 25 * mm, "width" : 150 * mm, "height" : 150 * mm});
        }
        {
            var Q0;
            Q0=qCreatedBy(id+"F28.planeOp",FACE);
            var sketch = newSketch(context, id + "F29", { "sketchPlane" : qUnion([Q0])});
            skPoint(sketch, "E137.0", {"position": v(8.92, 0.03) * mm});
            skPoint(sketch, "E138.0", {"position": v(4.38, -0.36) * mm});
            skPoint(sketch, "E139.0", {"position": v(4.38, -1.24) * mm});
            skPoint(sketch, "E140.0", {"position": v(8.92, -0.85) * mm});
            skLineSegment(sketch, "E141", {"start": v(4.38, -0.36) * mm, "end": v(4.38, -1.24) * mm, "construction": true});
            skLineSegment(sketch, "E142", {"start": v(6.62, -0.36) * mm, "end": v(4.38, -0.36) * mm, "construction": true});
            skLineSegment(sketch, "E143", {"start": v(6.14, -1.24) * mm, "end": v(4.38, -1.24) * mm, "construction": true});
            skFitSpline(sketch, "E144", {"points": [v(8.92, 0.03) * mm, v(4.38, -0.36) * mm], "startDerivative": vector(-3.96, -1.3) * mm, "endDerivative": vector(-7.11, 0) * mm});
            skFitSpline(sketch, "E145", {"points": [v(8.92, -0.85) * mm, v(4.38, -1.24) * mm], "startDerivative": vector(-3.81, -0.8) * mm, "endDerivative": vector(-6.87, 0) * mm});
            skSolve(sketch);
        }
        {
            var Q1;
            Q1 = qSketchRegion(id + "F24", true);
            var Q2;
            Q2 = qSketchRegion(id + "F25", true);
            var Q3;
            Q3=sQuery(id+"F27.wireOp",EDGE,"E136");
            var Q4;
            Q4=sQuery(id+"F27.wireOp",EDGE,"E135");
            var Q5;
            Q5=sQuery(id+"F29.wireOp",EDGE,"E144");
            var Q6;
            Q6=sQuery(id+"F29.wireOp",EDGE,"E145");
            loft(context, id + "F30", {"operationType" : NewBodyOperationType.REMOVE, "addGuides" : true, "sheetProfilesArray" : [{ "sheetProfileEntities" : qUnion([Q1]) }, { "sheetProfileEntities" : qUnion([Q2]) }], "guidesArray" : [{ "guideEntities" : qUnion([Q3]), "guideDerivativeType" : LoftGuideDerivativeType.DEFAULT, "guideDerivativeMagnitude" : 1 }, { "guideEntities" : qUnion([Q4]), "guideDerivativeType" : LoftGuideDerivativeType.DEFAULT, "guideDerivativeMagnitude" : 1 }, { "guideEntities" : qUnion([Q5]), "guideDerivativeType" : LoftGuideDerivativeType.DEFAULT, "guideDerivativeMagnitude" : 1 }, { "guideEntities" : qUnion([Q6]), "guideDerivativeType" : LoftGuideDerivativeType.DEFAULT, "guideDerivativeMagnitude" : 1 }]});
        }
        {
            var Q0;
            {var subQ0=sQuery(id+"F25.wireOp",EDGE,"E123.0");var subQ8=sQuery(id+"F25.wireOp",EDGE,"E122.0");Q0=makeQuery(id+"F30.boolean.opBoolean","COPY",FACE,{"derivedFrom":makeQuery(id+"F30.opLoft","CAP_FACE",FACE,{"disambiguationData":[OSD([makeQuery(id+"F25.imprint","IMPRINT",FACE,{"disambiguationData":[TD([[makeQuery(id+"F25.imprint","IMPRINT",EDGE,{"derivedFrom":subQ8}),1.0]])]}),makeQuery(id+"F25.imprint","IMPRINT",FACE,{"disambiguationData":[TD([[makeQuery(id+"F25.imprint","IMPRINT",EDGE,{"derivedFrom":subQ0}),1.0]])]})])],"isStart":true})});}
            extrude(context, id + "F31", {"entities" : qUnion([Q0]), "operationType" : NewBodyOperationType.REMOVE, "oppositeDirection" : true, "depth" : 3 * mm, "offsetDistance" : 25 * mm});
        }
        {
            var Q0;
            {var subQ0=sQuery(id+"F0.wireOp",EDGE,"E30");var subQ2=sQuery(id+"F0.wireOp",EDGE,"E12");var subQ4=sQuery(id+"F0.wireOp",EDGE,"E11.filletArc");var subQ6=sQuery(id+"F0.wireOp",EDGE,"E4.filletArc");var subQ8=sQuery(id+"F0.wireOp",EDGE,"E10");var subQ10=sQuery(id+"F0.wireOp",EDGE,"E0");var subQ11=makeQuery(id+"F1.opExtrude","SWEPT_FACE",FACE,{"disambiguationData":[OSD([subQ10])]});var subQ12=sQuery(id+"F0.wireOp",EDGE,"E3");var subQ14=sQuery(id+"F0.wireOp",EDGE,"E13.filletArc");var subQ16=sQuery(id+"F0.wireOp",EDGE,"E1");var subQ22=sQuery(id+"F0.wireOp",EDGE,"E2.filletArc");var subQ25=sQuery(id+"F0.wireOp",EDGE,"E7");var subQ26=sQuery(id+"F0.wireOp",EDGE,"E6");var subQ29=sQuery(id+"F0.wireOp",EDGE,"E21");var subQ30=sQuery(id+"F0.wireOp",EDGE,"E20");var subQ31=sQuery(id+"F0.wireOp",EDGE,"E19");var subQ32=sQuery(id+"F0.wireOp",EDGE,"E18");var subQ33=sQuery(id+"F0.wireOp",EDGE,"E17");var subQ34=sQuery(id+"F0.wireOp",EDGE,"E16");var subQ35=sQuery(id+"F0.wireOp",EDGE,"E15");var subQ36=sQuery(id+"F0.wireOp",EDGE,"E14");var subQ37=sQuery(id+"F0.wireOp",EDGE,"E22");var subQ38=sQuery(id+"F0.wireOp",EDGE,"E8");var subQ39=sQuery(id+"F0.wireOp",EDGE,"E9.filletArc");var subQ40=sQuery(id+"F0.wireOp",EDGE,"E23");var subQ41=sQuery(id+"F0.wireOp",EDGE,"E24");var subQ42=sQuery(id+"F0.wireOp",EDGE,"E25");var subQ43=sQuery(id+"F0.wireOp",EDGE,"E26");var subQ44=sQuery(id+"F0.wireOp",EDGE,"E27");var subQ45=sQuery(id+"F0.wireOp",EDGE,"E28");var subQ46=sQuery(id+"F0.wireOp",EDGE,"E29");Q0=makeQuery(id+"F30.boolean.opBoolean","SPLIT",FACE,{"disambiguationData":[TD([subQ11])],"derivedFrom":makeQuery(id+"F3.boolean.opBoolean","SPLIT",FACE,{"disambiguationData":[TD([subQ11])],"derivedFrom":makeQuery(id+"F1.opExtrude","CAP_FACE",FACE,{"disambiguationData":[OSD([subQ10,subQ16,subQ22,subQ12,subQ6,subQ26,subQ25,subQ38,subQ39,subQ8,subQ4,subQ2,subQ14,subQ36,subQ35,subQ34,subQ33,subQ32,subQ31,subQ30,subQ29,subQ37,subQ40,subQ41,subQ42,subQ43,subQ44,subQ45,subQ46,subQ0,sQuery(id+"F0.wireOp",EDGE,"E31")])],"isStart":true})})});}
            var sketch = newSketch(context, id + "F32", { "sketchPlane" : qUnion([Q0])});
            skLineSegment(sketch, "E146", {"start": v(-22.87, 2.96) * mm, "end": v(4.36, 2.5) * mm});
            skLineSegment(sketch, "E147", {"start": v(-22.87, 1.86) * mm, "end": v(4.36, 1.4) * mm});
            skLineSegment(sketch, "E148", {"start": v(-22.87, 2.96) * mm, "end": v(-22.87, 1.86) * mm});
            skLineSegment(sketch, "E149.0", {"start": v(4.36, 2.5) * mm, "end": v(4.36, 1.4) * mm});
            skPoint(sketch, "E150.orphan", {"position": v(4.36, -1.14) * mm});
            skPoint(sketch, "E151.orphan", {"position": v(4.36, -3.53) * mm});
            skSolve(sketch);
        }
        {
            var Q0;
            Q0 = qSketchRegion(id + "F32", true);
            extrude(context, id + "F33", {"entities" : qUnion([Q0]), "operationType" : NewBodyOperationType.REMOVE, "oppositeDirection" : true, "depth" : 0.79 * mm, "offsetDistance" : 25 * mm});
        }
        {
            var Q0;
            Q0=makeQuery(id+"F33.boolean.opBoolean","COPY",FACE,{"derivedFrom":makeQuery(id+"F33.opExtrude","SWEPT_FACE",FACE,{"disambiguationData":[OSD([sQuery(id+"F32.wireOp",EDGE,"E149.0")])]})});
            var sketch = newSketch(context, id + "F34", { "sketchPlane" : qUnion([Q0])});
            skLineSegment(sketch, "E152", {"start": v(1.4, 0) * mm, "end": v(0.65, 0) * mm});
            skLineSegment(sketch, "E153", {"start": v(0.65, 0) * mm, "end": v(1.4, 0.79) * mm});
            skLineSegment(sketch, "E154", {"start": v(1.4, 0.79) * mm, "end": v(1.4, 0) * mm});
            skSolve(sketch);
        }
        {
            var Q0;
            Q0=makeQuery(id+"F33.boolean.opBoolean","COPY",FACE,{"derivedFrom":makeQuery(id+"F33.opExtrude","CAP_FACE",FACE,{"disambiguationData":[OSD([sQuery(id+"F32.wireOp",EDGE,"E146"),sQuery(id+"F32.wireOp",EDGE,"E147"),sQuery(id+"F32.wireOp",EDGE,"E148"),sQuery(id+"F32.wireOp",EDGE,"E149.0")])],"isStart":false})});
            var sketch = newSketch(context, id + "F35", { "sketchPlane" : qUnion([Q0])});
            skLineSegment(sketch, "E155.0", {"start": v(-18.76, 1.8) * mm, "end": v(4.36, 1.4) * mm});
            skPoint(sketch, "E156.orphan", {"position": v(-17.5, 1.77) * mm});
            skSolve(sketch);
        }
        {
            var Q0;
            Q0 = qSketchRegion(id + "F34", true);
            var Q1;
            Q1=sQuery(id+"F35.wireOp",EDGE,"E155.0");
            sweep(context, id + "F36", {"operationType" : NewBodyOperationType.REMOVE, "profiles" : qUnion([Q0]), "path" : qUnion([Q1])});
        }
        {
            var Q0;
            Q0=qCreatedBy(id+"F23.planeOp",FACE);
            var sketch = newSketch(context, id + "F37", { "sketchPlane" : qUnion([Q0])});
            skLineSegment(sketch, "E157.0", {"start": v(2.5, 0) * mm, "end": v(0.65, 0) * mm});
            skLineSegment(sketch, "E158.0", {"start": v(2.5, 0.79) * mm, "end": v(2.5, -0.8) * mm});
            skLineSegment(sketch, "E159.0", {"start": v(1.4, 0.8) * mm, "end": v(-0.09, -0.8) * mm});
            skLineSegment(sketch, "E160", {"start": v(2.5, -0.8) * mm, "end": v(-0.09, -0.8) * mm});
            skSolve(sketch);
        }
        {
            var Q0;
            Q0=makeQuery(id+"F36.boolean.opBoolean","MERGE",FACE,{"derivedFrom":[makeQuery(id+"F33.boolean.opBoolean","COPY",FACE,{"derivedFrom":makeQuery(id+"F33.opExtrude","SWEPT_FACE",FACE,{"disambiguationData":[OSD([sQuery(id+"F32.wireOp",EDGE,"E149.0")])]})})],"fromTools":[makeQuery(id+"F36.opSweep","CAP_FACE",FACE,{"disambiguationData":[OSD([sQuery(id+"F34.wireOp",EDGE,"E152"),sQuery(id+"F34.wireOp",EDGE,"E153"),sQuery(id+"F34.wireOp",EDGE,"E154"),sQuery(id+"F35.wireOp",VERTEX,"E155.0.end")])],"isStart":true})]});
            var sketch = newSketch(context, id + "F38", { "sketchPlane" : qUnion([Q0])});
            skLineSegment(sketch, "E161.0.0", {"start": v(0.65, 0) * mm, "end": v(2.5, 0) * mm});
            skLineSegment(sketch, "E161.0.1", {"start": v(2.5, 0) * mm, "end": v(2.5, 0.79) * mm});
            skLineSegment(sketch, "E161.0.2", {"start": v(2.5, 0.79) * mm, "end": v(1.4, 0.79) * mm});
            skLineSegment(sketch, "E161.0.3", {"start": v(1.4, 0.8) * mm, "end": v(0.65, 0) * mm});
            skSolve(sketch);
        }
        {
            var Q1;
            Q1 = qSketchRegion(id + "F37", true);
            var Q2;
            Q2 = qSketchRegion(id + "F38", true);
            loft(context, id + "F39", {"operationType" : NewBodyOperationType.REMOVE, "endCondition" : LoftEndDerivativeType.NORMAL_TO_PROFILE, "endMagnitude" : 1, "sheetProfilesArray" : [{ "sheetProfileEntities" : qUnion([Q1]) }, { "sheetProfileEntities" : qUnion([Q2]) }]});
        }
        {
            var Q0;
            {var subQ0=sQuery(id+"F0.wireOp",EDGE,"E31");Q0=makeQuery(id+"F5.boolean.opBoolean","SPLIT",FACE,{"disambiguationData":[TD([makeQuery(id+"F1.opExtrude","SWEPT_FACE",FACE,{"disambiguationData":[OSD([subQ0])]})])],"derivedFrom":makeQuery(id+"F1.opExtrude","CAP_FACE",FACE,{"disambiguationData":[OSD([sQuery(id+"F0.wireOp",EDGE,"E0"),sQuery(id+"F0.wireOp",EDGE,"E1"),sQuery(id+"F0.wireOp",EDGE,"E2.filletArc"),sQuery(id+"F0.wireOp",EDGE,"E3"),sQuery(id+"F0.wireOp",EDGE,"E4.filletArc"),sQuery(id+"F0.wireOp",EDGE,"E6"),sQuery(id+"F0.wireOp",EDGE,"E7"),sQuery(id+"F0.wireOp",EDGE,"E8"),sQuery(id+"F0.wireOp",EDGE,"E9.filletArc"),sQuery(id+"F0.wireOp",EDGE,"E10"),sQuery(id+"F0.wireOp",EDGE,"E11.filletArc"),sQuery(id+"F0.wireOp",EDGE,"E12"),sQuery(id+"F0.wireOp",EDGE,"E13.filletArc"),sQuery(id+"F0.wireOp",EDGE,"E14"),sQuery(id+"F0.wireOp",EDGE,"E15"),sQuery(id+"F0.wireOp",EDGE,"E16"),sQuery(id+"F0.wireOp",EDGE,"E17"),sQuery(id+"F0.wireOp",EDGE,"E18"),sQuery(id+"F0.wireOp",EDGE,"E19"),sQuery(id+"F0.wireOp",EDGE,"E20"),sQuery(id+"F0.wireOp",EDGE,"E21"),sQuery(id+"F0.wireOp",EDGE,"E22"),sQuery(id+"F0.wireOp",EDGE,"E23"),sQuery(id+"F0.wireOp",EDGE,"E24"),sQuery(id+"F0.wireOp",EDGE,"E25"),sQuery(id+"F0.wireOp",EDGE,"E26"),sQuery(id+"F0.wireOp",EDGE,"E27"),sQuery(id+"F0.wireOp",EDGE,"E28"),sQuery(id+"F0.wireOp",EDGE,"E29"),sQuery(id+"F0.wireOp",EDGE,"E30"),subQ0])],"isStart":false})});}
            var sketch = newSketch(context, id + "F40", { "sketchPlane" : qUnion([Q0])});
            skText(sketch, "E162", { "text": "EUROPA", "fontName": "OpenSans-Bold.ttf"});
            skLineSegment(sketch, "E163", {"start": v(17.44, 7.32) * mm, "end": v(17.82, -11.98) * mm, "construction": true});
            skText(sketch, "E164", { "text": "2.0", "fontName": "OpenSans-Bold.ttf"});
            const initialGuessF40  = {"E162": [0.01745, 0.00695, 0.01969, -0.9998, 0.0024], "E164": [0.01366, 0.00191, 0.01969, -0.9998, 0.002]};
            skSetInitialGuess(sketch, initialGuessF40);
            skSolve(sketch);
        }
        {
            var Q0;
            Q0 = qSketchRegion(id + "F40", true);
            extrude(context, id + "F41", {"entities" : qUnion([Q0]), "operationType" : NewBodyOperationType.REMOVE, "oppositeDirection" : true, "depth" : 0.6 * mm, "offsetDistance" : 25 * mm});
        }
    });
